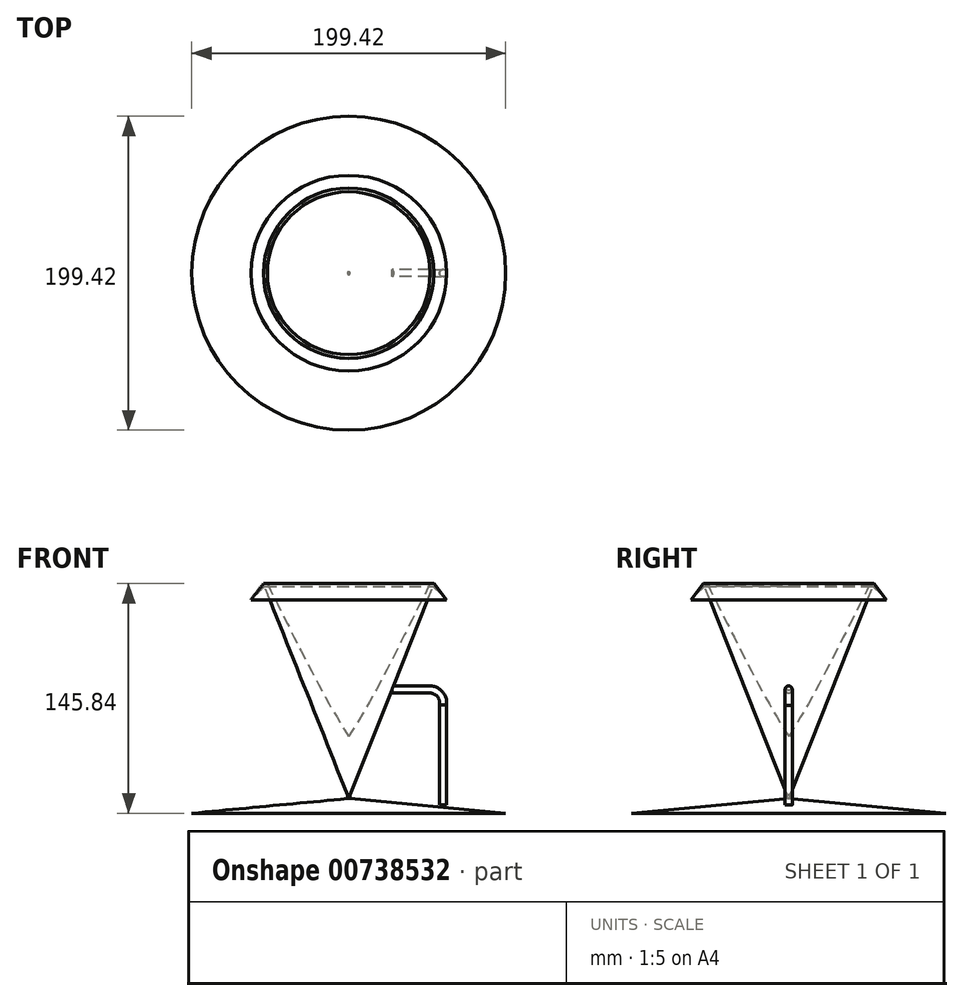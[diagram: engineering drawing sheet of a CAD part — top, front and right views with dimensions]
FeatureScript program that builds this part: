
annotation { "Feature Type Name" : "Feature", "Feature Type Description" : "" }
export const myFeature = defineFeature(function(context is Context, id is Id, definition is map)
    precondition{}
    {
        {
            var Q0;
            Q0=qCreatedBy(makeId("Front.planeOp"),FACE);
            var sketch = newSketch(context, id + "F0", { "sketchPlane" : qUnion([Q0])});
            skLineSegment(sketch, "E0", {"start": v(0, -161.55) * mm, "end": v(0, 114.48) * mm, "construction": true});
            skLineSegment(sketch, "E1", {"start": v(0, -23.53) * mm, "end": v(54.13, 112.91) * mm});
            skLineSegment(sketch, "E2", {"start": v(54.13, 112.91) * mm, "end": v(51.73, 112.91) * mm});
            skFitSpline(sketch, "E3", {"points": [v(51.73, 112.91) * mm, v(0, 15.97) * mm, v(-30.46, -9.36) * mm, v(-68.45, 32.53) * mm], "startDerivative": vector(-125.63, -247.73) * mm, "endDerivative": vector(-124.68, 195.16) * mm});
            skLineSegment(sketch, "E4", {"start": v(0, 15.97) * mm, "end": v(0, -23.53) * mm});
            skLineSegment(sketch, "E5", {"start": v(99.7, -32.93) * mm, "end": v(0, -23.53) * mm});
            skLineSegment(sketch, "E6", {"start": v(99.7, -32.93) * mm, "end": v(0, -32.93) * mm});
            skLineSegment(sketch, "E7", {"start": v(0, -32.93) * mm, "end": v(0, -23.53) * mm});
            skLineSegment(sketch, "E8", {"start": v(51.73, 112.91) * mm, "end": v(62.16, 102.66) * mm});
            skLineSegment(sketch, "E9", {"start": v(62.16, 102.66) * mm, "end": v(54.13, 112.91) * mm});
            skLineSegment(sketch, "E10", {"start": v(0.88, -21.32) * mm, "end": v(0.84, -23.61) * mm});
            skSolve(sketch);
        }
        {
            var Q0;
            Q0 = qSketchRegion(id + "F0", true);
            var Q1;
            Q1=sQuery(id+"F0.wireOp",EDGE,"E0");
            revolve(context, id + "F1", {"surfaceOperationType" : NewSurfaceOperationType.NEW, "entities" : qUnion([Q0]), "axis" : qUnion([Q1]), "revolveType" : RevolveType.FULL});
        }
        {
            var Q0;
            Q0=qCreatedBy(makeId("Front.planeOp"),FACE);
            var sketch = newSketch(context, id + "F2", { "sketchPlane" : qUnion([Q0])});
            skLineSegment(sketch, "E11", {"start": v(27.4, 45.44) * mm, "end": v(51.38, 45.44) * mm});
            skLineSegment(sketch, "E12", {"start": v(59.6, -27.63) * mm, "end": v(59.6, 35.85) * mm});
            skArc(sketch, "E13", {"start": v(59.6, 35.85) * mm, "mid": v(57.7, 42.54) * mm, "end": v(51.38, 45.44) * mm});
            skSolve(sketch);
        }
        {
            var Q0;
            Q0=sQuery(id+"F2.wireOp",EDGE,"E12");
            var Q1;
            Q1=sQuery(id+"F2.wireOp",VERTEX,"E12.start");
            cPlane(context, id + "F3", {"entities" : qUnion([Q0, Q1]), "cplaneType" : CPlaneType.CURVE_POINT, "offset" : 25 * mm, "width" : 150 * mm, "height" : 150 * mm});
        }
        {
            var Q0;
            Q0=qCreatedBy(id+"F3.planeOp",FACE);
            var sketch = newSketch(context, id + "F4", { "sketchPlane" : qUnion([Q0])});
            skCircle(sketch, "E14", {"center": v(59.88, 0) * mm, "radius": 2.26 * mm});
            skSolve(sketch);
        }
        {
            var Q0;
            Q0=makeQuery(id+"F4.imprint","IMPRINT",FACE,{"disambiguationData":[TD([[makeQuery(id+"F4.imprint","IMPRINT",EDGE,{"derivedFrom":sQuery(id+"F4.wireOp",EDGE,"E14")}),1.0]])]});
            var Q1;
            Q1=sQuery(id+"F2.wireOp",EDGE,"E11");
            var Q2;
            Q2=sQuery(id+"F2.wireOp",EDGE,"E13");
            var Q3;
            Q3=sQuery(id+"F2.wireOp",EDGE,"E12");
            sweep(context, id + "F5", {"operationType" : NewBodyOperationType.ADD, "profiles" : qUnion([Q0]), "path" : qUnion([Q1, Q2, Q3])});
        }
        {
            var Q0;
            Q0=qCreatedBy(makeId("Right.planeOp"),FACE);
            var sketch = newSketch(context, id + "F6", { "sketchPlane" : qUnion([Q0])});
            skLineSegment(sketch, "E15", {"start": v(-33.25, 62.3) * mm, "end": v(-52.36, 62.3) * mm});
            skLineSegment(sketch, "E16", {"start": v(-61.16, 51.22) * mm, "end": v(-61.16, 12.61) * mm});
            skLineSegment(sketch, "E17", {"start": v(-51.6, 0) * mm, "end": v(39.37, 0) * mm});
            skLineSegment(sketch, "E18", {"start": v(49.69, -10.7) * mm, "end": v(49.69, -26.37) * mm});
            skArc(sketch, "E19", {"start": v(-52.36, 62.3) * mm, "mid": v(-59.44, 58.88) * mm, "end": v(-61.16, 51.22) * mm});
            skArc(sketch, "E20", {"start": v(-61.16, 12.61) * mm, "mid": v(-58.5, 4.7) * mm, "end": v(-51.6, 0) * mm});
            skArc(sketch, "E21", {"start": v(49.69, -10.7) * mm, "mid": v(46.69, -3.27) * mm, "end": v(39.37, 0) * mm});
            skSolve(sketch);
        }
        {
            var Q0;
            Q0=sQuery(id+"F6.wireOp",EDGE,"E18");
            var Q1;
            Q1=sQuery(id+"F6.wireOp",VERTEX,"E18.end");
            cPlane(context, id + "F7", {"entities" : qUnion([Q0, Q1]), "cplaneType" : CPlaneType.CURVE_POINT, "offset" : 25 * mm, "width" : 150 * mm, "height" : 150 * mm});
        }
        {
            var Q0;
            Q0=qCreatedBy(id+"F7.planeOp",FACE);
            var sketch = newSketch(context, id + "F8", { "sketchPlane" : qUnion([Q0])});
            skCircle(sketch, "E22", {"center": v(0, -49.7) * mm, "radius": 1.74 * mm});
            skSolve(sketch);
        }
    });
